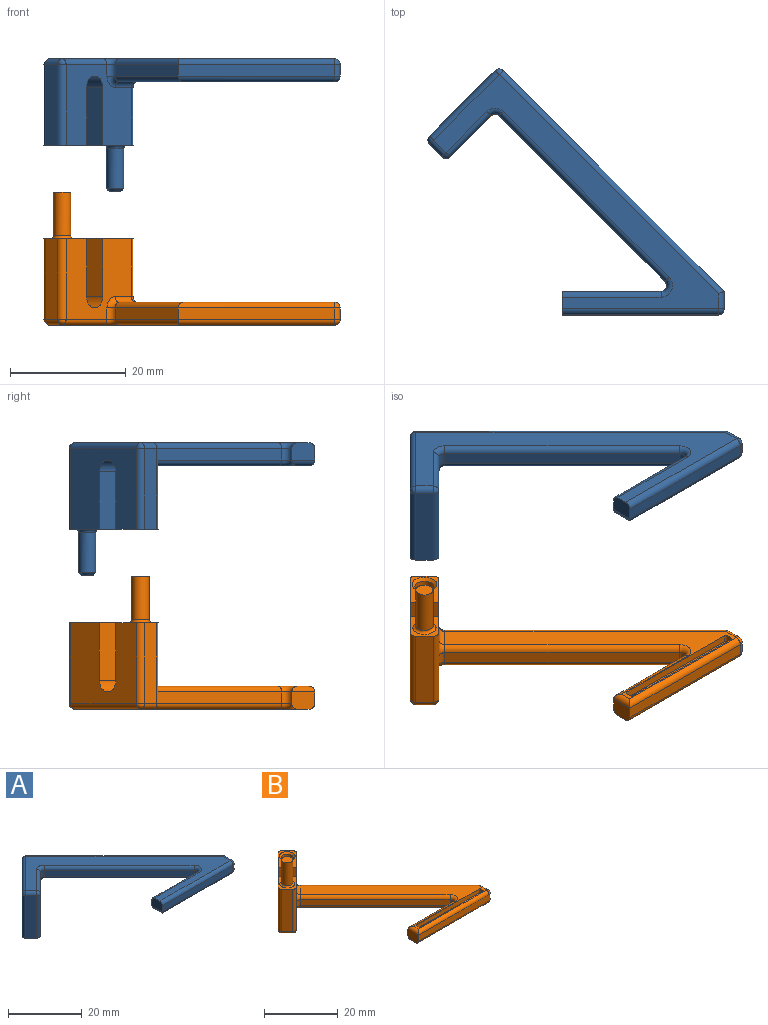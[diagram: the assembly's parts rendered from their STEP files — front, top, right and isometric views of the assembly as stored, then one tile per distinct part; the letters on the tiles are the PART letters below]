
ASSEMBLY  parts=2 mates=1
PART A: 66 faces, bbox 51.2x42.5x23 mm
  f0: plane 14x11.31mm, normal (-0.71,0.71,0), area 177.7mm2, adj f1,f23,f24,f25,f26,f28,f33,f34
  f1: plane 7.36x7.36mm, normal (0,0,-1), area 15mm2, adj f0,f21,f22,f26,f34,f43,f61
  f2: plane 37.18x36.94mm, normal (0,0,-1), area 209.7mm2, adj f9,f10,f11,f12,f14,f16,f17,f19
  f3: plane 28.7x28.7mm, normal (-0.71,-0.71,0), area 81.2mm2, adj f50,f51,f55,f56
  f4: plane 17.1x2mm, normal (0,1,0), area 34.2mm2, adj f5,f52,f56,f58
  f5: plane 4x3mm, normal (-1,0,0), area 11.6mm2, adj f4,f6,f8,f30,f48,f58
  f6: plane 27x2mm, normal (0,-1,0), area 54mm2, adj f5,f30,f38,f45
  f7: plane 3x2mm, normal (1,0,0), area 6mm2, adj f20,f29,f37,f38
  f8: plane 49.2x40.48mm, normal (0,0,1), area 305.3mm2, adj f5,f27,f29,f30,f33,f42,f49,f53
  f9: plane 1.5x1mm, normal (1,0,0), area 1.5mm2, adj f2,f13,f16,f17
  f10: plane 24x1.25mm, normal (0,1,0), area 30mm2, adj f2,f14,f15,f16
  f11: plane 1.5x1mm, normal (-1,0,0), area 1.5mm2, adj f2,f13,f14,f19
  f12: plane 24x1.25mm, normal (0,-1,0), area 30mm2, adj f2,f17,f18,f19
  f13: plane 24.5x1mm, normal (0,0,-1), area 24.5mm2, adj f9,f11,f15,f18
  f14: cylinder r=0.25mm len=1.5mm, axis (0,0,1), area 0.6mm2, adj f2,f10,f11,f15
  f15: cylinder r=0.25mm len=24.5mm, axis (1,0,0), area 9.5mm2, adj f10,f13,f14,f16
  f16: cylinder r=0.25mm len=1.5mm, axis (0,0,-1), area 0.6mm2, adj f2,f9,f10,f15
  f17: cylinder r=0.25mm len=1.5mm, axis (0,0,1), area 0.6mm2, adj f2,f9,f12,f18
  f18: cylinder r=0.25mm len=24.5mm, axis (-1,0,0), area 9.5mm2, adj f12,f13,f17,f19
  f19: cylinder r=0.25mm len=1.5mm, axis (0,0,-1), area 0.6mm2, adj f2,f11,f12,f18
  f20: plane 38.18x38.18mm, normal (0.71,0.71,0), area 144.9mm2, adj f7,f23,f27,f28,f35,f36,f40
  f21: plane 14x11.31mm, normal (0.71,-0.71,0), area 154.6mm2, adj f1,f23,f24,f25,f26,f35,f43,f44
  f22: plane 14x2.12mm, normal (-0.71,-0.71,0), area 42mm2, adj f1,f34,f42,f43
  f23: plane 8.78x8.78mm, normal (0,0,-1), area 27mm2, adj f0,f20,f21,f25,f28,f35,f64
  f24: cylinder r=2mm len=6.36mm, axis (0.71,-0.71,0), area 31.4mm2, adj f0,f21,f25,f26
  f25: plane 10x3.54mm, normal (-0.71,-0.71,0), area 50mm2, adj f0,f21,f23,f24
  f26: plane 10x3.54mm, normal (0.71,0.71,0), area 50mm2, adj f0,f1,f21,f24
  f27: cylinder r=1mm len=38.89mm, axis (-0.71,0.71,0), area 84.6mm2, adj f8,f20,f29,f31
  f28: cylinder r=1mm len=14mm, axis (0,0,1), area 22mm2, adj f0,f20,f23,f31
  f29: cylinder r=1mm len=3mm, axis (0,1,0), area 4.5mm2, adj f7,f8,f27,f32
  f30: cylinder r=1mm len=27mm, axis (1,0,0), area 42.4mm2, adj f5,f6,f8,f32
  f31: sphere r=1mm, area 1.6mm2, adj f27,f28,f33
  f32: sphere r=1mm, area 1.6mm2, adj f29,f30,f38
  f33: cylinder r=1mm len=12.02mm, axis (-0.71,-0.71,0), area 25.1mm2, adj f0,f8,f31,f39
  f34: cylinder r=1mm len=14mm, axis (0,0,1), area 22mm2, adj f0,f1,f22,f39
  f35: cylinder r=1mm len=10mm, axis (0,0,1), area 15.7mm2, adj f20,f21,f23,f40
  f36: cylinder r=1mm len=35.36mm, axis (0.71,-0.71,0), area 76.7mm2, adj f2,f20,f37,f40
  f37: cylinder r=1mm len=3mm, axis (0,-1,0), area 4.5mm2, adj f2,f7,f36,f41
  f38: cylinder r=1mm len=2mm, axis (0,0,1), area 3.1mm2, adj f6,f7,f32,f41
  f39: sphere r=1mm, area 1.6mm2, adj f33,f34,f42
  f40: torus R=2mm, axis (-0.71,-0.71,0), area 3.4mm2, adj f20,f35,f36,f44
  f41: sphere r=1mm, area 1.6mm2, adj f37,f38,f45
  f42: cylinder r=1mm len=2.83mm, axis (0.71,-0.71,0), area 4.7mm2, adj f8,f22,f39,f46
  f43: cylinder r=1mm len=14mm, axis (0,0,1), area 22mm2, adj f1,f21,f22,f46
  f44: cylinder r=1mm len=3.54mm, axis (-0.71,-0.71,0), area 6.3mm2, adj f2,f21,f40,f47
  f45: cylinder r=1mm len=27mm, axis (-1,0,0), area 41.8mm2, adj f2,f6,f41,f48
  f46: sphere r=1mm, area 1.6mm2, adj f42,f43,f49
  f47: torus R=2mm, axis (-0.71,0.71,0), area 3.4mm2, adj f21,f44,f50,f51
  f48: cylinder r=1mm len=4mm, axis (0,1,0), area 5.1mm2, adj f2,f5,f45,f52
  f49: cylinder r=1mm len=7.78mm, axis (0.71,0.71,0), area 15.7mm2, adj f8,f21,f46,f53
  f50: cylinder r=1mm len=2mm, axis (0,0,1), area 3.1mm2, adj f3,f21,f47,f53
  f51: cylinder r=1mm len=29.41mm, axis (-0.71,0.71,0), area 63.8mm2, adj f2,f3,f47,f54
  f52: cylinder r=1mm len=17.1mm, axis (1,0,0), area 26.3mm2, adj f2,f4,f48,f54
  f53: torus R=2mm, axis (0,0,-1), area 3.4mm2, adj f8,f49,f50,f55
  f54: torus R=2mm, axis (0,0,-1), area 5mm2, adj f2,f51,f52,f56
  f55: cylinder r=1mm len=29.41mm, axis (0.71,-0.71,0), area 63.8mm2, adj f3,f8,f53,f57
  f56: cylinder r=1mm len=2mm, axis (0,0,1), area 4.7mm2, adj f3,f4,f54,f57
  f57: torus R=2mm, axis (0,0,-1), area 5mm2, adj f8,f55,f56,f58
  f58: cylinder r=1mm len=17.1mm, axis (-1,0,0), area 26.9mm2, adj f4,f5,f8,f57
  f59: cylinder r=1.65mm len=9.5mm, axis (0,0,-1), area 98.5mm2, adj f60,f61
  f60: plane 3.3x3.3mm, normal (0,0,-1), area 8.6mm2, adj f59
  f61: cone r=1.65mm half-angle=45deg, axis (0,0,-1), area 8.4mm2, adj f1,f59
  f62: cylinder r=1.5mm len=7mm, axis (0,0,1), area 66mm2, adj f64,f65
  f63: plane 2x2mm, normal (0,0,-1), area 3.1mm2, adj f65
  f64: torus R=2mm, axis (0,0,1), area 8.3mm2, adj f23,f62
  f65: cone r=1mm half-angle=45deg, axis (0,0,1), area 5.6mm2, adj f62,f63
PART B: 65 faces, bbox 51.2x42.5x23 mm
  f0: plane 14x11.31mm, normal (-0.71,0.71,0), area 177.7mm2, adj f1,f23,f28,f29,f30,f32,f37,f38
  f1: plane 7.36x7.36mm, normal (0,0,1), area 17mm2, adj f0,f21,f22,f30,f38,f47,f63
  f2: plane 37.18x36.94mm, normal (0,0,1), area 209.7mm2, adj f9,f10,f11,f12,f14,f16,f17,f19
  f3: plane 28.7x28.7mm, normal (-0.71,-0.71,0), area 81.2mm2, adj f54,f55,f59,f60
  f4: plane 17.1x2mm, normal (0,1,0), area 34.2mm2, adj f5,f56,f60,f62
  f5: plane 4x3mm, normal (-1,0,0), area 11.6mm2, adj f4,f6,f8,f34,f52,f62
  f6: plane 27x2mm, normal (0,-1,0), area 54mm2, adj f5,f34,f42,f49
  f7: plane 3x2mm, normal (1,0,0), area 6mm2, adj f20,f33,f41,f42
  f8: plane 49.2x40.48mm, normal (0,0,-1), area 305.3mm2, adj f5,f31,f33,f34,f37,f46,f53,f57
  f9: plane 1.5x1mm, normal (1,0,0), area 1.5mm2, adj f2,f13,f16,f17
  f10: plane 24x1.25mm, normal (0,1,0), area 30mm2, adj f2,f14,f15,f16
  f11: plane 1.5x1mm, normal (-1,0,0), area 1.5mm2, adj f2,f13,f14,f19
  f12: plane 24x1.25mm, normal (0,-1,0), area 30mm2, adj f2,f17,f18,f19
  f13: plane 24.5x1mm, normal (0,0,1), area 24.5mm2, adj f9,f11,f15,f18
  f14: cylinder r=0.25mm len=1.5mm, axis (0,0,-1), area 0.6mm2, adj f2,f10,f11,f15
  f15: cylinder r=0.25mm len=24.5mm, axis (1,0,0), area 9.5mm2, adj f10,f13,f14,f16
  f16: cylinder r=0.25mm len=1.5mm, axis (0,0,1), area 0.6mm2, adj f2,f9,f10,f15
  f17: cylinder r=0.25mm len=1.5mm, axis (0,0,-1), area 0.6mm2, adj f2,f9,f12,f18
  f18: cylinder r=0.25mm len=24.5mm, axis (-1,0,0), area 9.5mm2, adj f12,f13,f17,f19
  f19: cylinder r=0.25mm len=1.5mm, axis (0,0,1), area 0.6mm2, adj f2,f11,f12,f18
  f20: plane 38.18x38.18mm, normal (0.71,0.71,0), area 144.9mm2, adj f7,f23,f31,f32,f39,f40,f44
  f21: plane 14x11.31mm, normal (0.71,-0.71,0), area 154.6mm2, adj f1,f23,f28,f29,f30,f39,f47,f48
  f22: plane 14x2.12mm, normal (-0.71,-0.71,0), area 42mm2, adj f1,f38,f46,f47
  f23: plane 8.78x8.78mm, normal (0,0,1), area 25mm2, adj f0,f20,f21,f29,f32,f39,f64
  f24: cylinder r=1.5mm len=7.5mm, axis (0,0,-1), area 70.7mm2, adj f25,f63
  f25: plane 3x3mm, normal (0,0,1), area 7.1mm2, adj f24
  f26: cylinder r=1.65mm len=9.5mm, axis (0,0,1), area 98.5mm2, adj f27,f64
  f27: plane 3.3x3.3mm, normal (0,0,1), area 8.6mm2, adj f26
  f28: cylinder r=2mm len=6.36mm, axis (0.71,-0.71,0), area 31.4mm2, adj f0,f21,f29,f30
  f29: plane 10x3.54mm, normal (-0.71,-0.71,0), area 50mm2, adj f0,f21,f23,f28
  f30: plane 10x3.54mm, normal (0.71,0.71,0), area 50mm2, adj f0,f1,f21,f28
  f31: cylinder r=1mm len=38.89mm, axis (-0.71,0.71,0), area 84.6mm2, adj f8,f20,f33,f35
  f32: cylinder r=1mm len=14mm, axis (0,0,-1), area 22mm2, adj f0,f20,f23,f35
  f33: cylinder r=1mm len=3mm, axis (0,1,0), area 4.5mm2, adj f7,f8,f31,f36
  f34: cylinder r=1mm len=27mm, axis (1,0,0), area 42.4mm2, adj f5,f6,f8,f36
  f35: sphere r=1mm, area 1.6mm2, adj f31,f32,f37
  f36: sphere r=1mm, area 1.6mm2, adj f33,f34,f42
  f37: cylinder r=1mm len=12.02mm, axis (-0.71,-0.71,0), area 25.1mm2, adj f0,f8,f35,f43
  f38: cylinder r=1mm len=14mm, axis (0,0,-1), area 22mm2, adj f0,f1,f22,f43
  f39: cylinder r=1mm len=10mm, axis (0,0,-1), area 15.7mm2, adj f20,f21,f23,f44
  f40: cylinder r=1mm len=35.36mm, axis (0.71,-0.71,0), area 76.7mm2, adj f2,f20,f41,f44
  f41: cylinder r=1mm len=3mm, axis (0,-1,0), area 4.5mm2, adj f2,f7,f40,f45
  f42: cylinder r=1mm len=2mm, axis (0,0,-1), area 3.1mm2, adj f6,f7,f36,f45
  f43: sphere r=1mm, area 1.6mm2, adj f37,f38,f46
  f44: torus R=2mm, axis (-0.71,-0.71,0), area 3.4mm2, adj f20,f39,f40,f48
  f45: sphere r=1mm, area 1.6mm2, adj f41,f42,f49
  f46: cylinder r=1mm len=2.83mm, axis (0.71,-0.71,0), area 4.7mm2, adj f8,f22,f43,f50
  f47: cylinder r=1mm len=14mm, axis (0,0,-1), area 22mm2, adj f1,f21,f22,f50
  f48: cylinder r=1mm len=3.54mm, axis (-0.71,-0.71,0), area 6.3mm2, adj f2,f21,f44,f51
  f49: cylinder r=1mm len=27mm, axis (-1,0,0), area 41.8mm2, adj f2,f6,f45,f52
  f50: sphere r=1mm, area 1.6mm2, adj f46,f47,f53
  f51: torus R=2mm, axis (-0.71,0.71,0), area 3.4mm2, adj f21,f48,f54,f55
  f52: cylinder r=1mm len=4mm, axis (0,1,0), area 5.1mm2, adj f2,f5,f49,f56
  f53: cylinder r=1mm len=7.78mm, axis (0.71,0.71,0), area 15.7mm2, adj f8,f21,f50,f57
  f54: cylinder r=1mm len=2mm, axis (0,0,-1), area 3.1mm2, adj f3,f21,f51,f57
  f55: cylinder r=1mm len=29.41mm, axis (-0.71,0.71,0), area 63.8mm2, adj f2,f3,f51,f58
  f56: cylinder r=1mm len=17.1mm, axis (1,0,0), area 26.3mm2, adj f2,f4,f52,f58
  f57: torus R=2mm, axis (0,0,1), area 3.4mm2, adj f8,f53,f54,f59
  f58: torus R=2mm, axis (0,0,1), area 5mm2, adj f2,f55,f56,f60
  f59: cylinder r=1mm len=29.41mm, axis (0.71,-0.71,0), area 63.8mm2, adj f3,f8,f57,f61
  f60: cylinder r=1mm len=2mm, axis (0,0,-1), area 4.7mm2, adj f3,f4,f58,f61
  f61: torus R=2mm, axis (0,0,1), area 5mm2, adj f8,f59,f60,f62
  f62: cylinder r=1mm len=17.1mm, axis (-1,0,0), area 26.9mm2, adj f4,f5,f8,f61
  f63: torus R=2mm, axis (0,0,-1), area 8.3mm2, adj f1,f24
  f64: cone r=1.65mm half-angle=45deg, axis (0,0,1), area 8.4mm2, adj f23,f26
PLACE A t=(4.15,-5.94,14.9)mm
PLACE B t=(4.15,-5.94,-1.22)mm fixed
MATE slider A.f59 <-> B.f24  axis (0,0,1) through (-15.93,24.23,30.4)mm
